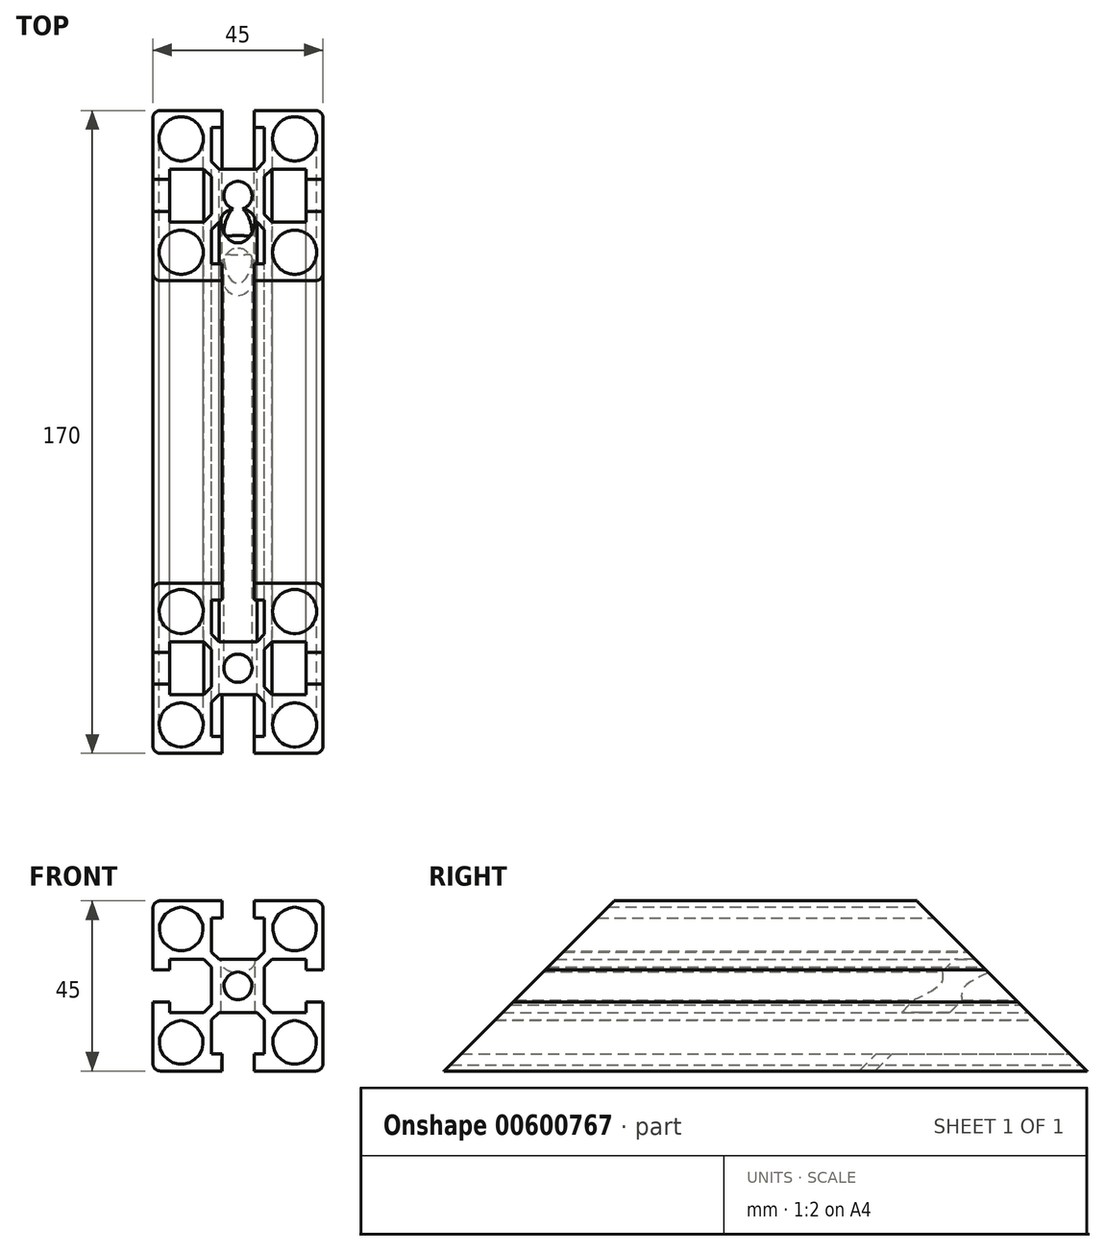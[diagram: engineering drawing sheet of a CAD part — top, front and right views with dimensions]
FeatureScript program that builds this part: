
annotation { "Feature Type Name" : "Feature", "Feature Type Description" : "" }
export const myFeature = defineFeature(function(context is Context, id is Id, definition is map)
    precondition{}
    {
        {
            var Q0;
            Q0=qCreatedBy(makeId("Front.planeOp"),FACE);
            var sketch = newSketch(context, id + "F0", { "sketchPlane" : qUnion([Q0])});
            skLineSegment(sketch, "E0.bottom", {"start": v(20.5, 22.5) * mm, "end": v(4.25, 22.5) * mm});
            skLineSegment(sketch, "E0.top", {"start": v(20.5, -22.5) * mm, "end": v(4.25, -22.5) * mm});
            skLineSegment(sketch, "E0.left", {"start": v(22.5, 20.5) * mm, "end": v(22.5, 4.25) * mm});
            skLineSegment(sketch, "E0.right", {"start": v(-22.5, 20.5) * mm, "end": v(-22.5, 4.25) * mm});
            skPoint(sketch, "E0.middle", {"position": v(0, 0) * mm});
            skCircle(sketch, "E1", {"center": v(-15, 15) * mm, "radius": 5.85 * mm});
            skCircle(sketch, "E2", {"center": v(15, 15) * mm, "radius": 5.85 * mm});
            skCircle(sketch, "E3", {"center": v(-15, -15) * mm, "radius": 5.85 * mm});
            skCircle(sketch, "E4", {"center": v(15, -15) * mm, "radius": 5.85 * mm});
            skLineSegment(sketch, "E5.bottom", {"start": v(-15, 15) * mm, "end": v(15, 15) * mm, "construction": true});
            skLineSegment(sketch, "E5.top", {"start": v(-15, -15) * mm, "end": v(15, -15) * mm, "construction": true});
            skLineSegment(sketch, "E5.left", {"start": v(-15, 15) * mm, "end": v(-15, -15) * mm, "construction": true});
            skLineSegment(sketch, "E5.right", {"start": v(15, 15) * mm, "end": v(15, -15) * mm, "construction": true});
            skPoint(sketch, "E6.visualSharp", {"position": v(-22.5, 22.5) * mm});
            skArc(sketch, "E6.filletArc", {"start": v(-20.5, 22.5) * mm, "mid": v(-21.91, 21.91) * mm, "end": v(-22.5, 20.5) * mm});
            skPoint(sketch, "E7.visualSharp", {"position": v(22.5, 22.5) * mm});
            skArc(sketch, "E7.filletArc", {"start": v(22.5, 20.5) * mm, "mid": v(21.91, 21.91) * mm, "end": v(20.5, 22.5) * mm});
            skPoint(sketch, "E8.visualSharp", {"position": v(22.5, -22.5) * mm});
            skArc(sketch, "E8.filletArc", {"start": v(20.5, -22.5) * mm, "mid": v(21.91, -21.91) * mm, "end": v(22.5, -20.5) * mm});
            skPoint(sketch, "E9.visualSharp", {"position": v(-22.5, -22.5) * mm});
            skArc(sketch, "E9.filletArc", {"start": v(-22.5, -20.5) * mm, "mid": v(-21.91, -21.91) * mm, "end": v(-20.5, -22.5) * mm});
            skLineSegment(sketch, "E10", {"start": v(-38.5, 0) * mm, "end": v(32.41, 0) * mm, "construction": true});
            skLineSegment(sketch, "E11", {"start": v(0, 24.68) * mm, "end": v(0, -32.45) * mm, "construction": true});
            skPoint(sketch, "E11.endSnap0", {"position": v(0, -15) * mm});
            skLineSegment(sketch, "E12", {"start": v(-4.25, 22.5) * mm, "end": v(-4.25, 18) * mm});
            skLineSegment(sketch, "E13", {"start": v(-4.25, 18) * mm, "end": v(-7, 18) * mm});
            skLineSegment(sketch, "E14", {"start": v(-7, 18) * mm, "end": v(-7, 9) * mm});
            skLineSegment(sketch, "E15", {"start": v(-7, 9) * mm, "end": v(-5, 7) * mm});
            skLineSegment(sketch, "E16", {"start": v(-5, 7) * mm, "end": v(5, 7) * mm});
            skLineSegment(sketch, "E17", {"start": v(5, 7) * mm, "end": v(7, 9) * mm});
            skLineSegment(sketch, "E18", {"start": v(7, 9) * mm, "end": v(7, 18) * mm});
            skLineSegment(sketch, "E19", {"start": v(7, 18) * mm, "end": v(4.25, 18) * mm});
            skLineSegment(sketch, "E20", {"start": v(4.25, 18) * mm, "end": v(4.25, 22.5) * mm});
            skLineSegment(sketch, "E21.1.0", {"start": v(-22.5, -4.25) * mm, "end": v(-18, -4.25) * mm});
            skLineSegment(sketch, "E21.1.1", {"start": v(-9, 7) * mm, "end": v(-18, 7) * mm});
            skLineSegment(sketch, "E21.1.2", {"start": v(-18, -7) * mm, "end": v(-9, -7) * mm});
            skLineSegment(sketch, "E21.1.3", {"start": v(-9, -7) * mm, "end": v(-7, -5) * mm});
            skLineSegment(sketch, "E21.1.4", {"start": v(-7, -5) * mm, "end": v(-7, 5) * mm});
            skLineSegment(sketch, "E21.1.5", {"start": v(-18, 7) * mm, "end": v(-18, 4.25) * mm});
            skLineSegment(sketch, "E21.1.6", {"start": v(-7, 5) * mm, "end": v(-9, 7) * mm});
            skLineSegment(sketch, "E21.1.7", {"start": v(-18, -4.25) * mm, "end": v(-18, -7) * mm});
            skLineSegment(sketch, "E21.1.8", {"start": v(-18, 4.25) * mm, "end": v(-22.5, 4.25) * mm});
            skLineSegment(sketch, "E21.2.0", {"start": v(4.25, -22.5) * mm, "end": v(4.25, -18) * mm});
            skLineSegment(sketch, "E21.2.1", {"start": v(-7, -9) * mm, "end": v(-7, -18) * mm});
            skLineSegment(sketch, "E21.2.2", {"start": v(7, -18) * mm, "end": v(7, -9) * mm});
            skLineSegment(sketch, "E21.2.3", {"start": v(7, -9) * mm, "end": v(5, -7) * mm});
            skLineSegment(sketch, "E21.2.4", {"start": v(5, -7) * mm, "end": v(-5, -7) * mm});
            skLineSegment(sketch, "E21.2.5", {"start": v(-7, -18) * mm, "end": v(-4.25, -18) * mm});
            skLineSegment(sketch, "E21.2.6", {"start": v(-5, -7) * mm, "end": v(-7, -9) * mm});
            skLineSegment(sketch, "E21.2.7", {"start": v(4.25, -18) * mm, "end": v(7, -18) * mm});
            skLineSegment(sketch, "E21.2.8", {"start": v(-4.25, -18) * mm, "end": v(-4.25, -22.5) * mm});
            skLineSegment(sketch, "E21.3.0", {"start": v(22.5, 4.25) * mm, "end": v(18, 4.25) * mm});
            skLineSegment(sketch, "E21.3.1", {"start": v(9, -7) * mm, "end": v(18, -7) * mm});
            skLineSegment(sketch, "E21.3.2", {"start": v(18, 7) * mm, "end": v(9, 7) * mm});
            skLineSegment(sketch, "E21.3.3", {"start": v(9, 7) * mm, "end": v(7, 5) * mm});
            skLineSegment(sketch, "E21.3.4", {"start": v(7, 5) * mm, "end": v(7, -5) * mm});
            skLineSegment(sketch, "E21.3.5", {"start": v(18, -7) * mm, "end": v(18, -4.25) * mm});
            skLineSegment(sketch, "E21.3.6", {"start": v(7, -5) * mm, "end": v(9, -7) * mm});
            skLineSegment(sketch, "E21.3.7", {"start": v(18, 4.25) * mm, "end": v(18, 7) * mm});
            skLineSegment(sketch, "E21.3.8", {"start": v(18, -4.25) * mm, "end": v(22.5, -4.25) * mm});
            skLineSegment(sketch, "E22.trimOffspring", {"start": v(-4.25, 22.5) * mm, "end": v(-20.5, 22.5) * mm});
            skLineSegment(sketch, "E23.trimOffspring", {"start": v(-22.5, -4.25) * mm, "end": v(-22.5, -20.5) * mm});
            skLineSegment(sketch, "E24.trimOffspring", {"start": v(-4.25, -22.5) * mm, "end": v(-20.5, -22.5) * mm});
            skLineSegment(sketch, "E25.trimOffspring", {"start": v(22.5, -4.25) * mm, "end": v(22.5, -20.5) * mm});
            skCircle(sketch, "E26", {"center": v(0, 0) * mm, "radius": 3.75 * mm});
            skSolve(sketch);
        }
        {
            var Q0;
            Q0 = qSketchRegion(id + "F0", true);
            extrude(context, id + "F1", {"entities" : qUnion([Q0]), "depth" : 170 * mm, "offsetDistance" : 25 * mm});
        }
        {
            var Q0;
            Q0=makeQuery(id+"F1.opExtrude","SWEPT_FACE",FACE,{"disambiguationData":[OSD([sQuery(id+"F0.wireOp",EDGE,"E25.trimOffspring")])]});
            var sketch = newSketch(context, id + "F2", { "sketchPlane" : qUnion([Q0])});
            skLineSegment(sketch, "E27", {"start": v(-170, -22.5) * mm, "end": v(-125, 22.5) * mm});
            skLineSegment(sketch, "E28", {"start": v(-85, 42.34) * mm, "end": v(-85, -56.09) * mm, "construction": true});
            skLineSegment(sketch, "E29", {"start": v(-170, -22.5) * mm, "end": v(-170, 22.5) * mm});
            skLineSegment(sketch, "E30", {"start": v(-170, 22.5) * mm, "end": v(-125, 22.5) * mm});
            skLineSegment(sketch, "E31.MirrorCS", {"start": v(0, 22.5) * mm, "end": v(-45, 22.5) * mm});
            skLineSegment(sketch, "E32.MirrorCS", {"start": v(0, -22.5) * mm, "end": v(-45, 22.5) * mm});
            skLineSegment(sketch, "E33.MirrorCS", {"start": v(0, -22.5) * mm, "end": v(0, 22.5) * mm});
            skSolve(sketch);
        }
        {
            var Q0;
            Q0 = qSketchRegion(id + "F2", true);
            extrude(context, id + "F3", {"entities" : qUnion([Q0]), "operationType" : NewBodyOperationType.REMOVE, "endBound" : BoundingType.THROUGH_ALL, "oppositeDirection" : true, "depth" : 25 * mm, "offsetDistance" : 25 * mm});
        }
        {
            var Q0;
            Q0=makeQuery(id+"F3.boolean.opBoolean","COPY",FACE,{"derivedFrom":makeQuery(id+"F3.opExtrude","SWEPT_FACE",FACE,{"disambiguationData":[OSD([sQuery(id+"F2.wireOp",EDGE,"E32.MirrorCS")])]})});
            var sketch = newSketch(context, id + "F4", { "sketchPlane" : qUnion([Q0])});
            skCircle(sketch, "E34", {"center": v(0, 25.23) * mm, "radius": 4.5 * mm});
            skPoint(sketch, "E34.centerSnap0", {"position": v(0, 25.8) * mm});
            skSolve(sketch);
        }
        {
            var Q0;
            Q0 = qSketchRegion(id + "F4", true);
            extrude(context, id + "F5", {"entities" : qUnion([Q0]), "operationType" : NewBodyOperationType.REMOVE, "endBound" : BoundingType.THROUGH_ALL, "oppositeDirection" : true, "depth" : 25 * mm, "offsetDistance" : 25 * mm});
        }
    });
